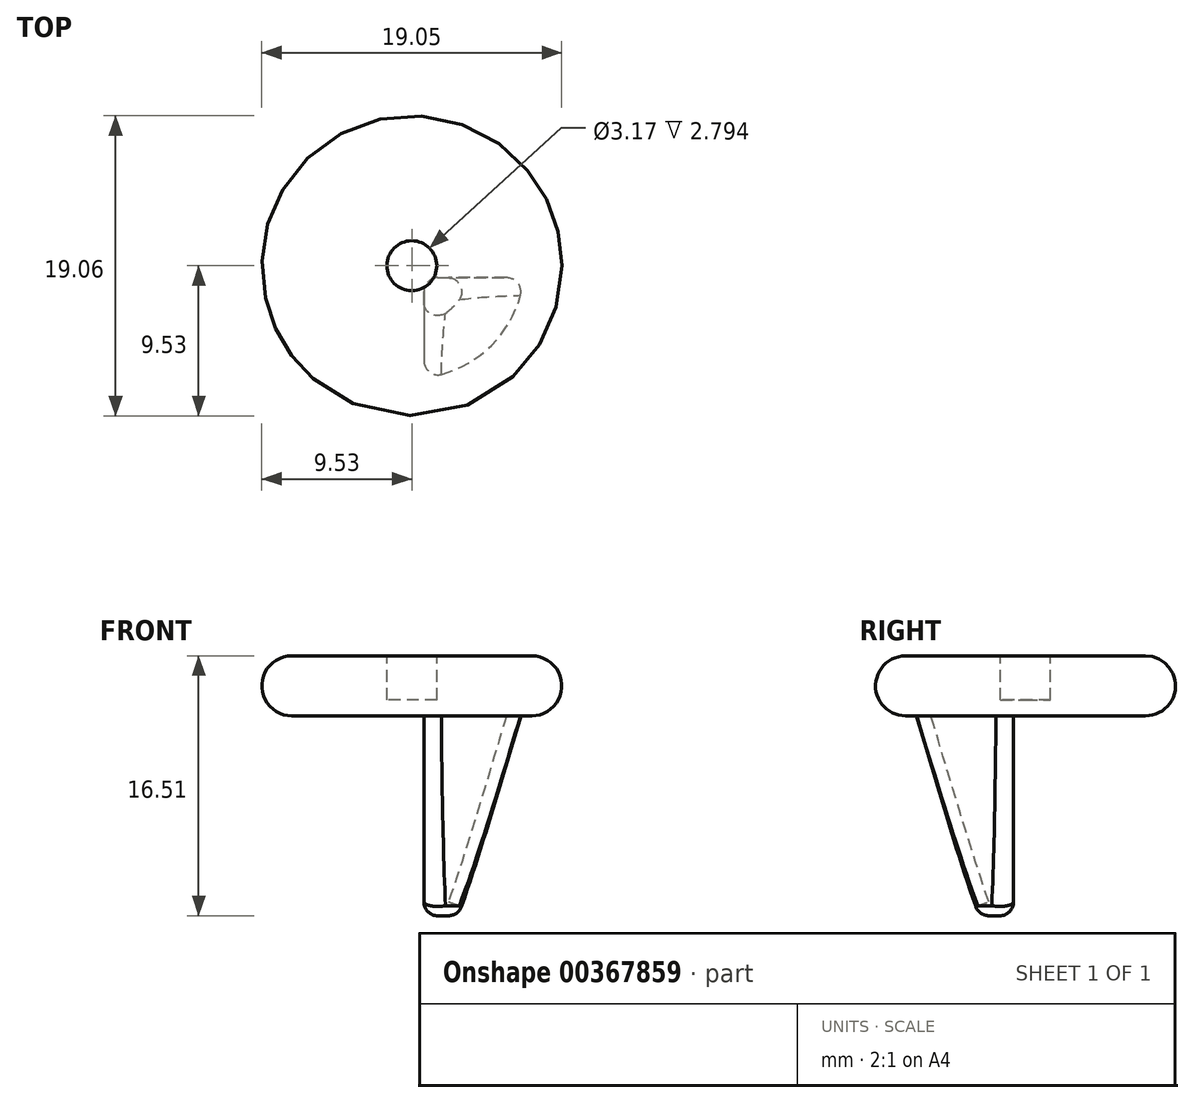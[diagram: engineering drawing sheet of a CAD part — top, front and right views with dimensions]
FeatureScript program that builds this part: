
annotation { "Feature Type Name" : "Feature", "Feature Type Description" : "" }
export const myFeature = defineFeature(function(context is Context, id is Id, definition is map)
    precondition{}
    {
        {
            var Q0;
            Q0=qCreatedBy(makeId("Top.planeOp"),FACE);
            var sketch = newSketch(context, id + "F0", { "sketchPlane" : qUnion([Q0])});
            skCircle(sketch, "E0", {"center": v(0, 0) * mm, "radius": 9.53 * mm});
            skSolve(sketch);
        }
        {
            var Q0;
            Q0 = qSketchRegion(id + "F0", true);
            extrude(context, id + "F1", {"entities" : qUnion([Q0]), "depth" : 3.8 * mm});
        }
        {
            var Q0;
            Q0=makeQuery(id+"F1.opExtrude","CAP_FACE",FACE,{"disambiguationData":[OSD([sQuery(id+"F0.wireOp",EDGE,"E0")])],"isStart":true});
            var sketch = newSketch(context, id + "F2", { "sketchPlane" : qUnion([Q0])});
            skLineSegment(sketch, "E1.bottom", {"start": v(0.76, 0.76) * mm, "end": v(7.11, 0.76) * mm});
            skLineSegment(sketch, "E1.left", {"start": v(0.76, 0.76) * mm, "end": v(0.76, 7.11) * mm});
            skCircle(sketch, "E2", {"center": v(0, 0) * mm, "radius": 7.15 * mm});
            skSolve(sketch);
        }
        {
            var Q0;
            Q0=makeQuery(id+"F2.imprint","IMPRINT",FACE,{"disambiguationData":[TD([[makeQuery(id+"F2.imprint","IMPRINT",EDGE,{"derivedFrom":makeQuery(id+"F1.opExtrude","CAP_EDGE",EDGE,{"disambiguationData":[OSD([sQuery(id+"F0.wireOp",EDGE,"E0")])],"isStart":true})}),-1.0]])]});
            cPlane(context, id + "F3", {"entities" : qUnion([Q0]), "cplaneType" : CPlaneType.OFFSET, "offset" : 12.7 * mm, "width" : 152.4 * mm, "height" : 152.4 * mm});
        }
        {
            var Q0;
            Q0=qCreatedBy(id+"F3.planeOp",FACE);
            var sketch = newSketch(context, id + "F4", { "sketchPlane" : qUnion([Q0])});
            skLineSegment(sketch, "E3.0", {"start": v(0.76, 0.76) * mm, "end": v(0.76, 3.44) * mm});
            skLineSegment(sketch, "E4.0", {"start": v(0.76, 0.76) * mm, "end": v(3.44, 0.76) * mm});
            skArc(sketch, "E5", {"start": v(3.44, 0.76) * mm, "mid": v(2.49, 2.49) * mm, "end": v(0.76, 3.44) * mm});
            skPoint(sketch, "E6.orphan", {"position": v(0.76, 7.11) * mm});
            skPoint(sketch, "E7.orphan", {"position": v(7.11, 0.76) * mm});
            skSolve(sketch);
        }
        {
            var Q1;
            {var subQ0=sQuery(id+"F2.wireOp",EDGE,"E1.bottom");Q1=makeQuery(id+"F2.imprint","IMPRINT",FACE,{"disambiguationData":[TD([[makeQuery(id+"F2.imprint","IMPRINT",EDGE,{"derivedFrom":subQ0}),1.0]])]});}
            var Q2;
            Q2=makeQuery(id+"F4.imprint","IMPRINT",FACE,{"disambiguationData":[TD([[makeQuery(id+"F4.imprint","IMPRINT",EDGE,{"derivedFrom":sQuery(id+"F4.wireOp",EDGE,"E3.0")}),-1.0]])]});
            loft(context, id + "F5", {"operationType" : NewBodyOperationType.ADD, "sheetProfilesArray" : [{ "sheetProfileEntities" : qUnion([Q1]) }, { "sheetProfileEntities" : qUnion([Q2]) }]});
        }
        {
            var Q0;
            {var subQ0=sQuery(id+"F4.wireOp",EDGE,"E4.0");var subQ1=sQuery(id+"F4.wireOp",EDGE,"E5");var subQ2=sQuery(id+"F4.wireOp",EDGE,"E3.0");Q0=makeQuery(id+"F5.opLoft","MID_CAP_EDGE",EDGE,{"disambiguationData":[OSD([subQ2,subQ0,subQ1]),TDD([makeQuery(id+"F4.imprint","INTERSECT",VERTEX,{"derivedFrom":[subQ2,subQ0]}),makeQuery(id+"F4.imprint","INTERSECT",VERTEX,{"derivedFrom":[subQ0,subQ1]}),makeQuery(id+"F4.imprint","IMPRINT",EDGE,{"derivedFrom":subQ0})])],"capPos":1.0});}
            var Q1;
            {var subQ0=sQuery(id+"F4.wireOp",EDGE,"E3.0");var subQ1=sQuery(id+"F4.wireOp",EDGE,"E5");var subQ2=sQuery(id+"F4.wireOp",EDGE,"E4.0");Q1=makeQuery(id+"F5.opLoft","MID_CAP_EDGE",EDGE,{"disambiguationData":[OSD([subQ0,subQ2,subQ1]),TDD([makeQuery(id+"F4.imprint","INTERSECT",VERTEX,{"derivedFrom":[subQ0,subQ2]}),makeQuery(id+"F4.imprint","INTERSECT",VERTEX,{"derivedFrom":[subQ0,subQ1]}),makeQuery(id+"F4.imprint","IMPRINT",EDGE,{"derivedFrom":subQ0})])],"capPos":1.0});}
            var Q2;
            {var subQ0=sQuery(id+"F4.wireOp",EDGE,"E5");var subQ1=sQuery(id+"F4.wireOp",EDGE,"E4.0");var subQ2=sQuery(id+"F4.wireOp",EDGE,"E3.0");Q2=makeQuery(id+"F5.opLoft","MID_CAP_EDGE",EDGE,{"disambiguationData":[OSD([subQ2,subQ1,subQ0]),TDD([makeQuery(id+"F4.imprint","INTERSECT",VERTEX,{"derivedFrom":[subQ2,subQ0]}),makeQuery(id+"F4.imprint","INTERSECT",VERTEX,{"derivedFrom":[subQ1,subQ0]}),makeQuery(id+"F4.imprint","IMPRINT",EDGE,{"derivedFrom":subQ0})])],"capPos":1.0});}
            var Q3;
            Q3=makeQuery(id+"F5.opLoft","SWEPT_EDGE",EDGE,{"disambiguationData":[OSD([sQuery(id+"F2.wireOp",EDGE,"E1.bottom"),sQuery(id+"F2.wireOp",EDGE,"E2"),sQuery(id+"F4.wireOp",EDGE,"E4.0"),sQuery(id+"F4.wireOp",EDGE,"E5")])]});
            var Q4;
            Q4=makeQuery(id+"F5.opLoft","SWEPT_EDGE",EDGE,{"disambiguationData":[OSD([sQuery(id+"F2.wireOp",EDGE,"E1.bottom"),sQuery(id+"F2.wireOp",EDGE,"E1.left"),sQuery(id+"F4.wireOp",EDGE,"E3.0"),sQuery(id+"F4.wireOp",EDGE,"E4.0")])]});
            var Q5;
            Q5=makeQuery(id+"F5.opLoft","SWEPT_EDGE",EDGE,{"disambiguationData":[OSD([sQuery(id+"F2.wireOp",EDGE,"E1.left"),sQuery(id+"F2.wireOp",EDGE,"E2"),sQuery(id+"F4.wireOp",EDGE,"E3.0"),sQuery(id+"F4.wireOp",EDGE,"E5")])]});
            fillet(context, id + "F6", {"entities" : qUnion([Q0, Q1, Q2, Q3, Q4, Q5]), "radius" : 0.89 * mm, "tangentPropagation" : true, "allowEdgeOverflow" : false});
        }
        {
            var Q0;
            Q0=makeQuery(id+"F1.opExtrude","CAP_FACE",FACE,{"disambiguationData":[OSD([sQuery(id+"F0.wireOp",EDGE,"E0")])],"isStart":false});
            var sketch = newSketch(context, id + "F7", { "sketchPlane" : qUnion([Q0])});
            skCircle(sketch, "E8", {"center": v(0, 0) * mm, "radius": 1.59 * mm});
            skSolve(sketch);
        }
        {
            var Q0;
            Q0=makeQuery(id+"F7.imprint","IMPRINT",FACE,{"disambiguationData":[TD([[makeQuery(id+"F7.imprint","IMPRINT",EDGE,{"derivedFrom":sQuery(id+"F7.wireOp",EDGE,"E8")}),1.0]])]});
            extrude(context, id + "F8", {"entities" : qUnion([Q0]), "operationType" : NewBodyOperationType.REMOVE, "oppositeDirection" : true, "depth" : 2.8 * mm});
        }
        {
            var Q0;
            Q0=makeQuery(id+"F1.opExtrude","CAP_EDGE",EDGE,{"disambiguationData":[OSD([sQuery(id+"F0.wireOp",EDGE,"E0")])],"isStart":true});
            var Q1;
            Q1=makeQuery(id+"F1.opExtrude","CAP_EDGE",EDGE,{"disambiguationData":[OSD([sQuery(id+"F0.wireOp",EDGE,"E0")])],"isStart":false});
            fillet(context, id + "F9", {"entities" : qUnion([Q0, Q1]), "radius" : 1.9 * mm, "tangentPropagation" : true, "allowEdgeOverflow" : false});
        }
    });
